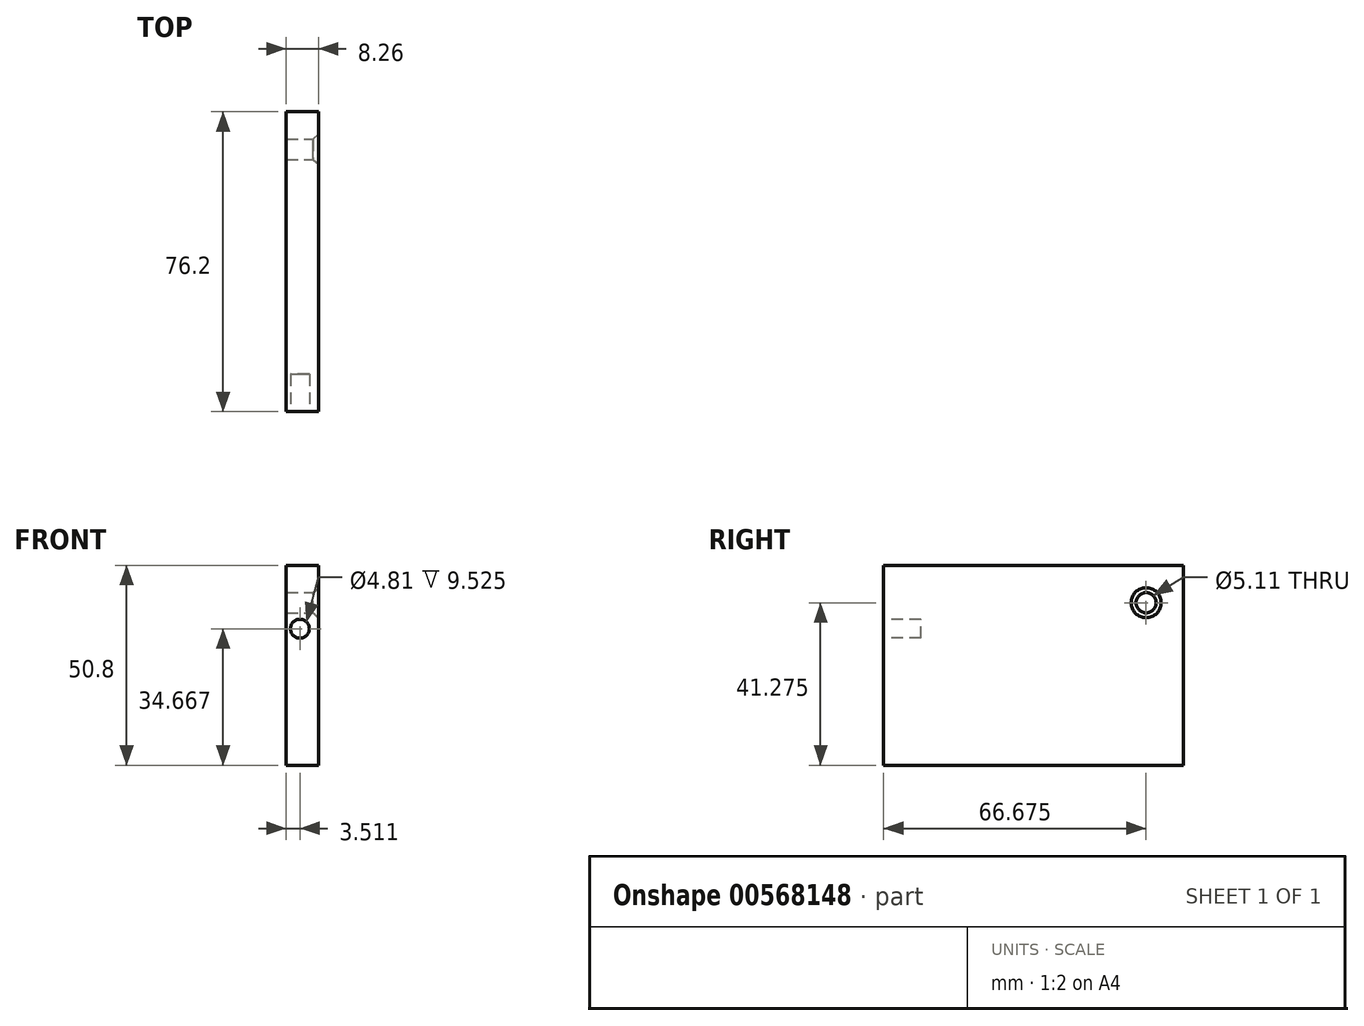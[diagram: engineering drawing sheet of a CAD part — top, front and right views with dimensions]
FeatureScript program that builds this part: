
annotation { "Feature Type Name" : "Feature", "Feature Type Description" : "" }
export const myFeature = defineFeature(function(context is Context, id is Id, definition is map)
    precondition{}
    {
        {
            var Q0;
            Q0=qCreatedBy(makeId("Right.planeOp"),FACE);
            var sketch = newSketch(context, id + "F0", { "sketchPlane" : qUnion([Q0])});
            skLineSegment(sketch, "E0.bottom", {"start": v(38.1, 25.4) * mm, "end": v(-38.1, 25.4) * mm});
            skLineSegment(sketch, "E0.top", {"start": v(38.1, -25.4) * mm, "end": v(-38.1, -25.4) * mm});
            skLineSegment(sketch, "E0.left", {"start": v(38.1, 25.4) * mm, "end": v(38.1, -25.4) * mm});
            skLineSegment(sketch, "E0.right", {"start": v(-38.1, 25.4) * mm, "end": v(-38.1, -25.4) * mm});
            skPoint(sketch, "E0.middle", {"position": v(0, 0) * mm});
            skSolve(sketch);
        }
        {
            var Q0;
            Q0 = qSketchRegion(id + "F0", true);
            extrude(context, id + "F1", {"entities" : qUnion([Q0]), "depth" : 8.25 * mm, "offsetDistance" : 25.4 * mm});
        }
        {
            var Q0;
            Q0=makeQuery(id+"F1.opExtrude","SWEPT_FACE",FACE,{"disambiguationData":[OSD([sQuery(id+"F0.wireOp",EDGE,"E0.right")])]});
            var sketch = newSketch(context, id + "F2", { "sketchPlane" : qUnion([Q0])});
            skCircle(sketch, "E1", {"center": v(3.51, 9.27) * mm, "radius": 2.4 * mm});
            skSolve(sketch);
        }
        {
            var Q0;
            Q0 = qSketchRegion(id + "F2", true);
            extrude(context, id + "F3", {"entities" : qUnion([Q0]), "operationType" : NewBodyOperationType.REMOVE, "oppositeDirection" : true, "depth" : 9.52 * mm, "offsetDistance" : 25.4 * mm});
        }
        {
            var Q0;
            Q0=makeQuery(id+"F1.opExtrude","CAP_FACE",FACE,{"disambiguationData":[OSD([sQuery(id+"F0.wireOp",EDGE,"E0.bottom"),sQuery(id+"F0.wireOp",EDGE,"E0.top"),sQuery(id+"F0.wireOp",EDGE,"E0.left"),sQuery(id+"F0.wireOp",EDGE,"E0.right")])],"isStart":false});
            var sketch = newSketch(context, id + "F4", { "sketchPlane" : qUnion([Q0])});
            skPoint(sketch, "E2", {"position": v(28.57, 15.88) * mm});
            skSolve(sketch);
        }
        {
            var Q0;
            Q0=sQuery(id+"F4.wireOp",VERTEX,"E2");
            var Q1;
            Q1=makeQuery(id+"F1.opExtrude","SWEPT_BODY",BODY,{"disambiguationData":[OSD([sQuery(id+"F0.wireOp",EDGE,"E0.bottom"),sQuery(id+"F0.wireOp",EDGE,"E0.top"),sQuery(id+"F0.wireOp",EDGE,"E0.left"),sQuery(id+"F0.wireOp",EDGE,"E0.right")])]});
            hole(context, id + "F5", {"style" : HoleStyle.C_SINK, "endStyle" : HoleEndStyle.THROUGH, "holeDiameter" : 5.1 * mm, "cSinkDiameter" : 7.62 * mm, "cSinkAngle" : 82 * degree, "isTappedThrough" : true, "tappedDepth" : 12.7 * mm, "tapClearance" : 3, "locations" : qUnion([Q0]), "scope" : qUnion([Q1])});
        }
    });
